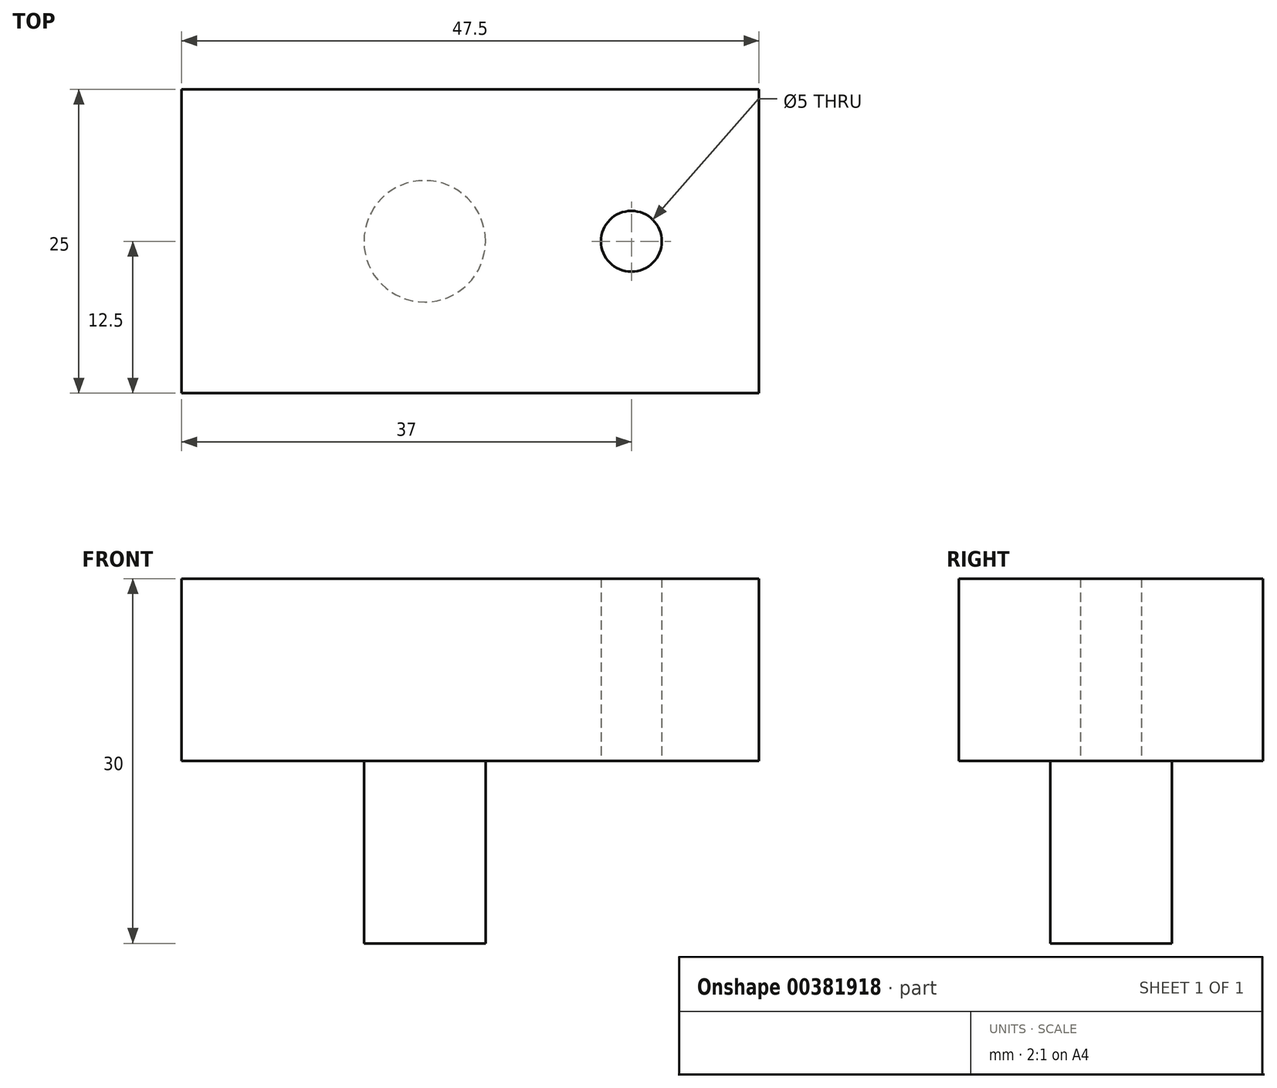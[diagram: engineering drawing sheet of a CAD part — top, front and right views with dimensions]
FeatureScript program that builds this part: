
annotation { "Feature Type Name" : "Feature", "Feature Type Description" : "" }
export const myFeature = defineFeature(function(context is Context, id is Id, definition is map)
    precondition{}
    {
        {
            var Q0;
            Q0=qCreatedBy(makeId("Top.planeOp"),FACE);
            var sketch = newSketch(context, id + "F0", { "sketchPlane" : qUnion([Q0])});
            skLineSegment(sketch, "E0.bottom", {"start": v(0, 0) * mm, "end": v(160, 0) * mm, "construction": true});
            skLineSegment(sketch, "E0.top", {"start": v(0, 80) * mm, "end": v(160, 80) * mm, "construction": true});
            skLineSegment(sketch, "E0.left", {"start": v(0, 0) * mm, "end": v(0, 80) * mm, "construction": true});
            skLineSegment(sketch, "E0.right", {"start": v(160, 0) * mm, "end": v(160, 80) * mm, "construction": true});
            skArc(sketch, "E1", {"start": v(15, 20) * mm, "mid": v(10, 15) * mm, "end": v(15, 10) * mm, "construction": true});
            skLineSegment(sketch, "E2", {"start": v(0, 15) * mm, "end": v(160, 15) * mm, "construction": true});
            skArc(sketch, "E3", {"start": v(145, 10) * mm, "mid": v(150, 15) * mm, "end": v(145, 20) * mm, "construction": true});
            skLineSegment(sketch, "E4", {"start": v(15, 20) * mm, "end": v(145, 20) * mm, "construction": true});
            skLineSegment(sketch, "E5", {"start": v(145, 10) * mm, "end": v(15, 10) * mm, "construction": true});
            skCircle(sketch, "E6", {"center": v(130, 50) * mm, "radius": 4 * mm});
            skCircle(sketch, "E7", {"center": v(130, 50) * mm, "radius": 17.5 * mm});
            skArc(sketch, "E8", {"start": v(20, 55) * mm, "mid": v(15, 50) * mm, "end": v(20, 45) * mm, "construction": true});
            skArc(sketch, "E9", {"start": v(46, 45) * mm, "mid": v(51, 50) * mm, "end": v(46, 55) * mm, "construction": true});
            skLineSegment(sketch, "E10", {"start": v(20, 50) * mm, "end": v(46, 50) * mm, "construction": true});
            skLineSegment(sketch, "E11", {"start": v(20, 55) * mm, "end": v(46, 55) * mm, "construction": true});
            skLineSegment(sketch, "E12", {"start": v(20, 45) * mm, "end": v(46, 45) * mm, "construction": true});
            skLineSegment(sketch, "E13.bottom", {"start": v(0, 0) * mm, "end": v(30, 0) * mm});
            skLineSegment(sketch, "E13.top", {"start": v(0, 32.5) * mm, "end": v(30, 32.5) * mm});
            skLineSegment(sketch, "E13.left", {"start": v(0, 0) * mm, "end": v(0, 32.5) * mm});
            skLineSegment(sketch, "E13.right", {"start": v(30, 0) * mm, "end": v(30, 32.5) * mm});
            skCircle(sketch, "E14", {"center": v(15, 15) * mm, "radius": 5 * mm});
            skLineSegment(sketch, "E15", {"start": v(30, 32.5) * mm, "end": v(160, 32.5) * mm});
            skLineSegment(sketch, "E16", {"start": v(160, 32.5) * mm, "end": v(160, 22.5) * mm});
            skLineSegment(sketch, "E17", {"start": v(160, 22.5) * mm, "end": v(30, 22.5) * mm});
            skCircle(sketch, "E18", {"center": v(143, 50) * mm, "radius": 2.5 * mm});
            skLineSegment(sketch, "E19.bottom", {"start": v(73.5, 62.5) * mm, "end": v(18.5, 62.5) * mm});
            skLineSegment(sketch, "E19.top", {"start": v(73.5, 37.5) * mm, "end": v(18.5, 37.5) * mm});
            skLineSegment(sketch, "E19.left", {"start": v(73.5, 62.5) * mm, "end": v(73.5, 37.5) * mm});
            skLineSegment(sketch, "E19.right", {"start": v(18.5, 62.5) * mm, "end": v(18.5, 37.5) * mm});
            skCircle(sketch, "E20", {"center": v(63, 50) * mm, "radius": 2.5 * mm});
            skCircle(sketch, "E21", {"center": v(46, 50) * mm, "radius": 5 * mm});
            skLineSegment(sketch, "E22.0", {"start": v(26, 62.5) * mm, "end": v(26, 37.5) * mm});
            skSolve(sketch);
        }
        {
            var Q0;
            {var subQ0=sQuery(id+"F0.wireOp",EDGE,"E19.left");Q0=makeQuery(id+"F0.imprint","IMPRINT",FACE,{"disambiguationData":[TD([[makeQuery(id+"F0.imprint","IMPRINT",EDGE,{"derivedFrom":subQ0}),-1.0]])]});}
            var Q1;
            Q1=makeQuery(id+"F0.imprint","IMPRINT",FACE,{"disambiguationData":[TD([[makeQuery(id+"F0.imprint","IMPRINT",EDGE,{"derivedFrom":sQuery(id+"F0.wireOp",EDGE,"E21")}),1.0]])]});
            extrude(context, id + "F1", {"entities" : qUnion([Q0, Q1]), "depth" : (15) * mm});
        }
        {
            var Q0;
            Q0=makeQuery(id+"F0.imprint","IMPRINT",FACE,{"disambiguationData":[TD([[makeQuery(id+"F0.imprint","IMPRINT",EDGE,{"derivedFrom":sQuery(id+"F0.wireOp",EDGE,"E21")}),1.0]])]});
            extrude(context, id + "F2", {"entities" : qUnion([Q0]), "operationType" : NewBodyOperationType.ADD, "oppositeDirection" : true, "depth" : (15) * mm});
        }
    });
